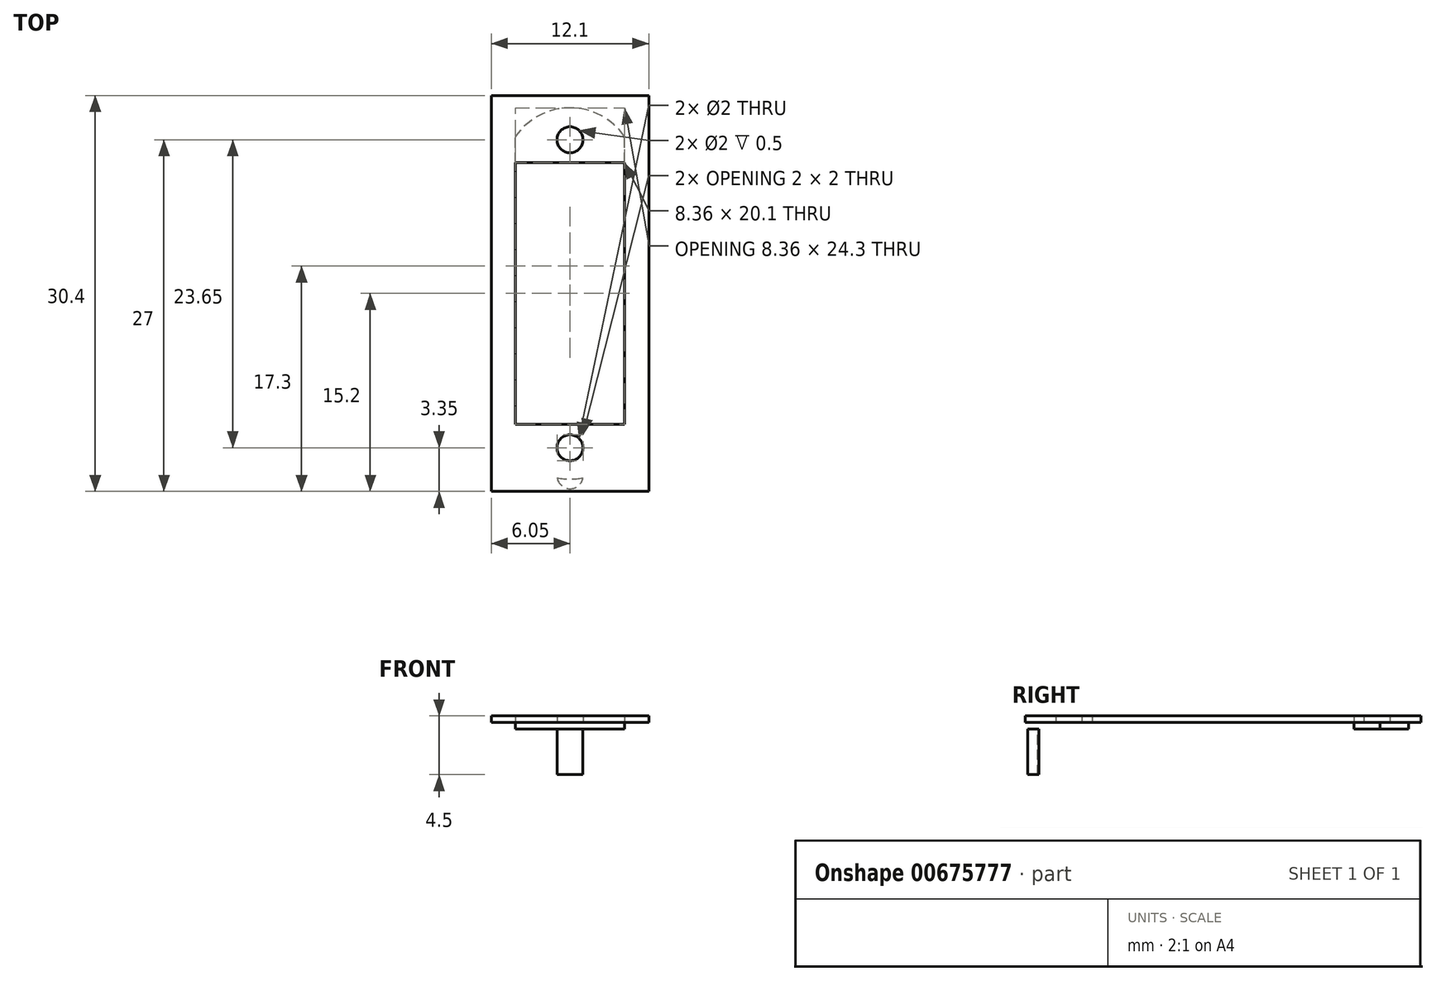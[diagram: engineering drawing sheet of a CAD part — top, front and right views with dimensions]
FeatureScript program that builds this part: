
annotation { "Feature Type Name" : "Feature", "Feature Type Description" : "" }
export const myFeature = defineFeature(function(context is Context, id is Id, definition is map)
    precondition{}
    {
        {
            var Q0;
            Q0=qCreatedBy(makeId("Top.planeOp"),FACE);
            var sketch = newSketch(context, id + "F0", { "sketchPlane" : qUnion([Q0])});
            skLineSegment(sketch, "E0.bottom", {"start": v(4.18, 0) * mm, "end": v(6.05, 0) * mm});
            skLineSegment(sketch, "E0.top", {"start": v(0, 11.7) * mm, "end": v(6.05, 11.7) * mm});
            skLineSegment(sketch, "E0.left", {"start": v(0, 0) * mm, "end": v(0, 11.7) * mm});
            skLineSegment(sketch, "E0.right", {"start": v(6.05, 0) * mm, "end": v(6.05, 11.7) * mm});
            skLineSegment(sketch, "E1.top", {"start": v(0, 10.05) * mm, "end": v(4.18, 10.05) * mm});
            skLineSegment(sketch, "E1.left", {"start": v(0, 0) * mm, "end": v(0, 10.05) * mm});
            skLineSegment(sketch, "E1.right", {"start": v(4.18, 0) * mm, "end": v(4.18, 10.05) * mm});
            skLineSegment(sketch, "E2.top", {"start": v(0, 15.2) * mm, "end": v(6.05, 15.2) * mm});
            skLineSegment(sketch, "E2.left", {"start": v(0, 0) * mm, "end": v(0, 15.2) * mm});
            skLineSegment(sketch, "E2.right", {"start": v(6.05, 0) * mm, "end": v(6.05, 15.2) * mm});
            skLineSegment(sketch, "E3.MirrorCS", {"start": v(-6.05, 0) * mm, "end": v(-6.05, 15.2) * mm});
            skLineSegment(sketch, "E4.MirrorCS", {"start": v(-4.18, 0) * mm, "end": v(-4.18, 10.05) * mm});
            skLineSegment(sketch, "E5.MirrorCS", {"start": v(0, 10.05) * mm, "end": v(-4.18, 10.05) * mm});
            skLineSegment(sketch, "E6.MirrorCS", {"start": v(0, 11.7) * mm, "end": v(-6.05, 11.7) * mm});
            skLineSegment(sketch, "E7.MirrorCS", {"start": v(0, 15.2) * mm, "end": v(-6.05, 15.2) * mm});
            skLineSegment(sketch, "E8.MirrorCS", {"start": v(0, -15.2) * mm, "end": v(6.05, -15.2) * mm});
            skLineSegment(sketch, "E9.MirrorCS", {"start": v(0, -15.2) * mm, "end": v(-6.05, -15.2) * mm});
            skLineSegment(sketch, "E10.MirrorCS", {"start": v(0, -11.7) * mm, "end": v(-6.05, -11.7) * mm});
            skLineSegment(sketch, "E11.MirrorCS", {"start": v(0, -11.7) * mm, "end": v(6.05, -11.7) * mm});
            skLineSegment(sketch, "E12.MirrorCS", {"start": v(0, -10.05) * mm, "end": v(4.18, -10.05) * mm});
            skLineSegment(sketch, "E13.MirrorCS", {"start": v(0, -10.05) * mm, "end": v(-4.18, -10.05) * mm});
            skLineSegment(sketch, "E14.MirrorCS", {"start": v(-4.18, 0) * mm, "end": v(-4.18, -10.05) * mm});
            skLineSegment(sketch, "E15.MirrorCS", {"start": v(4.18, 0) * mm, "end": v(4.18, -10.05) * mm});
            skLineSegment(sketch, "E16.MirrorCS", {"start": v(-6.05, 0) * mm, "end": v(-6.05, -15.2) * mm});
            skLineSegment(sketch, "E17.MirrorCS", {"start": v(6.05, 0) * mm, "end": v(6.05, -15.2) * mm});
            skSolve(sketch);
        }
        {
            var Q0;
            {var subQ3=sQuery(id+"F0.wireOp",EDGE,"E8.MirrorCS");Q0=makeQuery(id+"F0.imprint","IMPRINT",FACE,{"disambiguationData":[TD([[makeQuery(id+"F0.imprint","IMPRINT",EDGE,{"derivedFrom":subQ3}),1.0]])]});}
            var Q1;
            {var subQ0=sQuery(id+"F0.wireOp",EDGE,"E0.top");Q1=makeQuery(id+"F0.imprint","IMPRINT",FACE,{"disambiguationData":[TD([[makeQuery(id+"F0.imprint","IMPRINT",EDGE,{"derivedFrom":subQ0}),1.0]])]});}
            var Q2;
            {var subQ0=sQuery(id+"F0.wireOp",EDGE,"E6.MirrorCS");Q2=makeQuery(id+"F0.imprint","IMPRINT",FACE,{"disambiguationData":[TD([[makeQuery(id+"F0.imprint","IMPRINT",EDGE,{"derivedFrom":subQ0}),-1.0]])]});}
            var Q3;
            {var subQ2=sQuery(id+"F0.wireOp",EDGE,"E0.top");Q3=makeQuery(id+"F0.imprint","IMPRINT",FACE,{"disambiguationData":[TD([[makeQuery(id+"F0.imprint","IMPRINT",EDGE,{"derivedFrom":subQ2}),-1.0]])]});}
            var Q4;
            {var subQ4=sQuery(id+"F0.wireOp",EDGE,"E0.bottom");Q4=makeQuery(id+"F0.imprint","IMPRINT",FACE,{"disambiguationData":[TD([[makeQuery(id+"F0.imprint","IMPRINT",EDGE,{"derivedFrom":subQ4}),-1.0]])]});}
            extrude(context, id + "F1", {"entities" : qUnion([Q0, Q1, Q2, Q3, Q4]), "depth" : 1 * mm, "offsetDistance" : 25 * mm});
        }
        {
            var Q0;
            Q0=makeQuery(id+"F1.opExtrude","CAP_FACE",FACE,{"disambiguationData":[OSD([sQuery(id+"F0.wireOp",EDGE,"E1.top"),sQuery(id+"F0.wireOp",EDGE,"E1.right"),sQuery(id+"F0.wireOp",EDGE,"E2.top"),sQuery(id+"F0.wireOp",EDGE,"E2.right"),sQuery(id+"F0.wireOp",EDGE,"E3.MirrorCS"),sQuery(id+"F0.wireOp",EDGE,"E4.MirrorCS"),sQuery(id+"F0.wireOp",EDGE,"E5.MirrorCS"),sQuery(id+"F0.wireOp",EDGE,"E7.MirrorCS"),sQuery(id+"F0.wireOp",EDGE,"E8.MirrorCS"),sQuery(id+"F0.wireOp",EDGE,"E9.MirrorCS"),sQuery(id+"F0.wireOp",EDGE,"E12.MirrorCS"),sQuery(id+"F0.wireOp",EDGE,"E13.MirrorCS"),sQuery(id+"F0.wireOp",EDGE,"E14.MirrorCS"),sQuery(id+"F0.wireOp",EDGE,"E15.MirrorCS"),sQuery(id+"F0.wireOp",EDGE,"E16.MirrorCS"),sQuery(id+"F0.wireOp",EDGE,"E17.MirrorCS")])],"isStart":false});
            var sketch = newSketch(context, id + "F2", { "sketchPlane" : qUnion([Q0])});
            skLineSegment(sketch, "E18", {"start": v(4.2, 10.05) * mm, "end": v(4.2, 12.05) * mm});
            skLineSegment(sketch, "E19.MirrorCS", {"start": v(-4.2, 10.05) * mm, "end": v(-4.2, 12.05) * mm});
            skArc(sketch, "E20", {"start": v(4.2, 12.05) * mm, "mid": v(0, 14.15) * mm, "end": v(-4.2, 12.05) * mm});
            skLineSegment(sketch, "E21.MirrorCS", {"start": v(-4.2, -10.05) * mm, "end": v(-4.2, -12.05) * mm});
            skArc(sketch, "E22.MirrorCS", {"start": v(4.2, -12.05) * mm, "mid": v(0, -14.15) * mm, "end": v(-4.2, -12.05) * mm});
            skLineSegment(sketch, "E23.MirrorCS", {"start": v(4.2, -10.05) * mm, "end": v(4.2, -12.05) * mm});
            skLineSegment(sketch, "E24", {"start": v(-4.18, 10.05) * mm, "end": v(4.2, 10.05) * mm});
            skLineSegment(sketch, "E25", {"start": v(-4.18, -10.05) * mm, "end": v(4.2, -10.05) * mm});
            skSolve(sketch);
        }
        {
            var Q0;
            Q0=makeQuery(id+"F1.opExtrude","CAP_FACE",FACE,{"disambiguationData":[OSD([sQuery(id+"F0.wireOp",EDGE,"E1.top"),sQuery(id+"F0.wireOp",EDGE,"E1.right"),sQuery(id+"F0.wireOp",EDGE,"E2.top"),sQuery(id+"F0.wireOp",EDGE,"E2.right"),sQuery(id+"F0.wireOp",EDGE,"E3.MirrorCS"),sQuery(id+"F0.wireOp",EDGE,"E4.MirrorCS"),sQuery(id+"F0.wireOp",EDGE,"E5.MirrorCS"),sQuery(id+"F0.wireOp",EDGE,"E7.MirrorCS"),sQuery(id+"F0.wireOp",EDGE,"E8.MirrorCS"),sQuery(id+"F0.wireOp",EDGE,"E9.MirrorCS"),sQuery(id+"F0.wireOp",EDGE,"E12.MirrorCS"),sQuery(id+"F0.wireOp",EDGE,"E13.MirrorCS"),sQuery(id+"F0.wireOp",EDGE,"E14.MirrorCS"),sQuery(id+"F0.wireOp",EDGE,"E15.MirrorCS"),sQuery(id+"F0.wireOp",EDGE,"E16.MirrorCS"),sQuery(id+"F0.wireOp",EDGE,"E17.MirrorCS")])],"isStart":true});
            var sketch = newSketch(context, id + "F3", { "sketchPlane" : qUnion([Q0])});
            skLineSegment(sketch, "E26", {"start": v(4.18, 10.05) * mm, "end": v(4.18, 12.05) * mm});
            skLineSegment(sketch, "E27", {"start": v(-4.18, 10.05) * mm, "end": v(-4.18, 12.05) * mm});
            skArc(sketch, "E28", {"start": v(4.18, 12.05) * mm, "mid": v(0, 14.25) * mm, "end": v(-4.18, 12.05) * mm});
            skArc(sketch, "E29.MirrorCS", {"start": v(4.18, -12.05) * mm, "mid": v(0, -14.25) * mm, "end": v(-4.18, -12.05) * mm});
            skLineSegment(sketch, "E30.MirrorCS", {"start": v(4.18, -10.05) * mm, "end": v(4.18, -12.05) * mm});
            skLineSegment(sketch, "E31.MirrorCS", {"start": v(-4.18, -10.05) * mm, "end": v(-4.18, -12.05) * mm});
            skSolve(sketch);
        }
        {
            var Q0;
            Q0 = qSketchRegion(id + "F3", true);
            var Q1;
            Q1=makeQuery(id+"F3.imprint","IMPRINT",FACE,{"disambiguationData":[TD([[makeQuery(id+"F3.imprint","IMPRINT",EDGE,{"derivedFrom":sQuery(id+"F3.wireOp",EDGE,"E26")}),1.0]])]});
            var Q2;
            Q2=makeQuery(id+"F3.imprint","IMPRINT",FACE,{"disambiguationData":[TD([[makeQuery(id+"F3.imprint","IMPRINT",EDGE,{"derivedFrom":sQuery(id+"F3.wireOp",EDGE,"E29.MirrorCS")}),-1.0]])]});
            extrude(context, id + "F4", {"entities" : qUnion([Q0, Q1, Q2]), "operationType" : NewBodyOperationType.REMOVE, "oppositeDirection" : true, "depth" : 0.5 * mm, "offsetDistance" : 25 * mm});
        }
        {
            var Q0;
            Q0=makeQuery(id+"F4.boolean.opBoolean","COPY",FACE,{"derivedFrom":makeQuery(id+"F4.opExtrude","CAP_FACE",FACE,{"disambiguationData":[OSD([sQuery(id+"F0.wireOp",EDGE,"E12.MirrorCS"),sQuery(id+"F0.wireOp",EDGE,"E13.MirrorCS"),sQuery(id+"F3.wireOp",EDGE,"E26"),sQuery(id+"F3.wireOp",EDGE,"E27"),sQuery(id+"F3.wireOp",EDGE,"E28")])],"isStart":false})});
            var sketch = newSketch(context, id + "F5", { "sketchPlane" : qUnion([Q0])});
            skCircle(sketch, "E32", {"center": v(0, 11.85) * mm, "radius": 1 * mm});
            skCircle(sketch, "E33", {"center": v(0, -11.8) * mm, "radius": 1 * mm});
            skSolve(sketch);
        }
        {
            var Q0;
            Q0=makeQuery(id+"F5.imprint","IMPRINT",FACE,{"disambiguationData":[TD([[makeQuery(id+"F5.imprint","IMPRINT",EDGE,{"derivedFrom":sQuery(id+"F5.wireOp",EDGE,"E32")}),1.0]])]});
            var Q1;
            Q1=makeQuery(id+"F5.imprint","IMPRINT",FACE,{"disambiguationData":[TD([[makeQuery(id+"F5.imprint","IMPRINT",EDGE,{"derivedFrom":sQuery(id+"F5.wireOp",EDGE,"E33")}),1.0]])]});
            extrude(context, id + "F6", {"entities" : qUnion([Q0, Q1]), "operationType" : NewBodyOperationType.REMOVE, "oppositeDirection" : true, "depth" : 25 * mm, "offsetDistance" : 25 * mm});
        }
        {
            var Q0;
            Q0=qCreatedBy(makeId("Top.planeOp"),FACE);
            var sketch = newSketch(context, id + "F7", { "sketchPlane" : qUnion([Q0])});
            skArc(sketch, "E34", {"start": v(-0.99, -14.16) * mm, "mid": v(0, -15) * mm, "end": v(0.99, -14.16) * mm});
            skPoint(sketch, "E35", {"position": v(-0.99, -14.16) * mm});
            skPoint(sketch, "E36", {"position": v(0.99, -14.16) * mm});
            skArc(sketch, "E37", {"start": v(-0.99, -14.16) * mm, "mid": v(0, -14.26) * mm, "end": v(0.99, -14.16) * mm});
            skArc(sketch, "E38.MirrorCS", {"start": v(-0.99, 14.16) * mm, "mid": v(0, 15) * mm, "end": v(0.99, 14.16) * mm});
            skPoint(sketch, "E39.MirrorP", {"position": v(0.99, 14.16) * mm});
            skPoint(sketch, "E40.MirrorP", {"position": v(-0.99, 14.16) * mm});
            skArc(sketch, "E41.MirrorCS", {"start": v(-0.99, 14.16) * mm, "mid": v(0, 14.26) * mm, "end": v(0.99, 14.16) * mm});
            skSolve(sketch);
        }
        {
            var Q0;
            Q0=makeQuery(id+"F7.imprint","IMPRINT",FACE,{"disambiguationData":[TD([[makeQuery(id+"F7.imprint","IMPRINT",EDGE,{"derivedFrom":sQuery(id+"F7.wireOp",EDGE,"E34")}),1.0]])]});
            var Q1;
            Q1=makeQuery(id+"F7.imprint","IMPRINT",FACE,{"disambiguationData":[TD([[makeQuery(id+"F7.imprint","IMPRINT",EDGE,{"derivedFrom":sQuery(id+"F7.wireOp",EDGE,"E38.MirrorCS")}),-1.0]])]});
            var Q2;
            Q2=sQuery(id+"F7.wireOp",EDGE,"E34");
            extrude(context, id + "F8", {"entities" : qUnion([Q0, Q1]), "operationType" : NewBodyOperationType.ADD, "surfaceEntities" : qUnion([Q2]), "oppositeDirection" : true, "depth" : 3.5 * mm, "offsetDistance" : 25 * mm});
        }
    });
